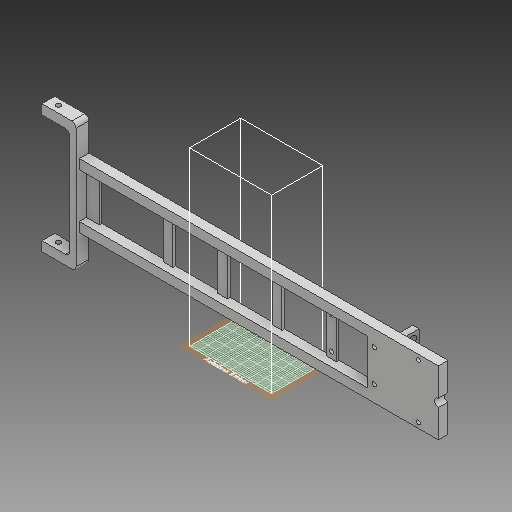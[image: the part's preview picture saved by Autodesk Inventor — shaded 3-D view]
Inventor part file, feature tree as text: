
AUTODESK INVENTOR PART (.ipt)
format: ipt  version: 2018 (Build 220112000, 112)  size: 669,184 bytes
history: native  units: mm
features: sketch x36, extrude x27, fillet x10, hole x6
ambient origin geometry x8: Origin, YZ Plane, XZ Plane, XY Plane, X Axis, Y Axis, Z Axis, Center Point
bodies: Solid1 (feature_tree)
feature tree (79):
  extrude  "Extrusion1"  Depth=50.0mm
  hole  "Hole1"  [1 undecoded]
  hole  "Hole2"  [1 undecoded]
  extrude  "Extrusion2"  Depth=25.0mm
  extrude  "Extrusion3"  Depth=25.0mm
  extrude  "Extrusion4"  Depth=5.0mm
  sketch  "Sketch7"  dims[d25=10.0mm d26=5.0mm]
  extrude  "Extrusion5"  Depth=5.0mm
  extrude  "Extrusion6"  Depth=35.0mm
  extrude  "Extrusion7"  Depth=35.0mm
  extrude  "Extrusion8"  Depth=35.0mm
  extrude  "Extrusion9"  Depth=2.0mm TaperAngle=0.0deg
  extrude  "Extrusion10"  Depth=7.5mm TaperAngle=0.0deg
  extrude  "Extrusion11"  Depth=10.0mm
  extrude  "Extrusion12"  Depth=7.5mm
  fillet  "Fillet1"  Radius=7.5mm
  fillet  "Fillet2"  Radius=25.0mm
  fillet  "Fillet3"  Radius=3.0mm
  fillet  "Fillet4"  Radius=3.2mm
  fillet  "Fillet5"  Radius=2.1mm
  fillet  "Fillet6"  Radius=5.5mm
  extrude  "Extrusion13"  Depth=92.5mm TaperAngle=0.0deg
  sketch  "Sketch17"  dims[d58=4.25mm d59=241.0mm d60=0.0mm]
  hole  "Hole3"  [1 undecoded]
  hole  "Hole4"  [1 undecoded]
  extrude  "Extrusion14"  Depth=5.0mm
  extrude  "Extrusion15"  Depth=91.25mm TaperAngle=0.0deg
  extrude  "Extrusion16"  Depth=30.0mm
  extrude  "Extrusion17"  Depth=2.5mm
  extrude  "Extrusion18"  Depth=14.55mm TaperAngle=0.0deg
  extrude  "Extrusion19"  Depth=0.1mm
  extrude  "Extrusion20"  Depth=3.25mm
  extrude  "Extrusion21"  Depth=3.25mm
  hole  "Hole5"  [1 undecoded]
  extrude  "Extrusion22"  Depth=2.0mm
  extrude  "Extrusion23"  Depth=15.0mm
  extrude  "Extrusion24"  Depth=10.0mm TaperAngle=0.0deg
  extrude  "Extrusion25"  Depth=2.0mm
  extrude  "Extrusion26"  Depth=100.0mm TaperAngle=0.0deg
  sketch  "Sketch34"  dims[d113=5.0mm d114=2.0mm d115=0.0mm]
  hole  "Hole6"  [1 undecoded]
  extrude  "Extrusion27"  Depth=5.5mm
  fillet  "Fillet7"  Radius=3.3mm
  fillet  "Fillet8"  Radius=3.3mm
  fillet  "Fillet9"  Radius=2.0mm
  fillet  "Fillet10"  Radius=5.5mm
  sketch  "Sketch1"  dims[d0=50.0mm d1=50.0mm]
  sketch  "Sketch2"  dims[d2=240.0mm d3=7.5mm]
  sketch  "Sketch3"  dims[d4=7.5mm d5=7.5mm d6=0.0mm]
  sketch  "Sketch4"  dims[d7=6.35mm d8=6.0mm d9=4.0mm d10=2.0mm d11=90.0deg d12=8.0mm d13=20.594885mm d14=25.0mm]
  sketch  "Sketch5"  dims[d15=3.3mm d16=6.0mm d17=4.0mm d18=2.0mm d19=90.0deg d20=8.0mm d21=20.594885mm d22=25.0mm]
  sketch  "Sketch6"  dims[d23=180.0deg d24=5.0mm]
  sketch  "Sketch8"  dims[d27=17.5mm d28=0.0mm d30=35.0mm]
  sketch  "Sketch9"  dims[d31=35.0mm d32=35.0mm]
  sketch  "Sketch10"  dims[d33=35.0mm d34=35.0mm]
  sketch  "Sketch11"  dims[d35=35.0mm d36=2.0mm d37=0.0mm]
  sketch  "Sketch12"  dims[d38=10.0mm d39=7.5mm d40=0.0mm]
  sketch  "Sketch13"  dims[d41=100.0mm d42=10.0mm]
  sketch  "Sketch14"  dims[d43=7.5mm d44=0.0mm d45=7.5mm d46=7.5mm d47=25.0mm d48=0.0mm d49=3.0mm d50=3.2mm d51=2.1mm d52=5.5mm]
  sketch  "Sketch15"  dims[d53=3.3mm d54=92.5mm d55=0.0mm]
  sketch  "Sketch16"  dims[d56=5.5mm d57=3.3mm]
  sketch  "Sketch18"  dims[d61=4.44mm d62=5.0mm]
  sketch  "Sketch19"  dims[d63=2.5mm d64=91.25mm d65=0.0mm]
  sketch  "Sketch20"  dims[d66=30.0mm d67=6.35mm]
  sketch  "Sketch21"  dims[d68=3.8mm d69=0.0mm d70=2.5mm]
  sketch  "Sketch22"  dims[d71=14.55mm d72=0.0mm d73=14.55mm d74=0.0mm]
  sketch  "Sketch23"  dims[d75=0.1mm d76=0.1mm]
  sketch  "Sketch24"  dims[d77=3.25mm d78=3.25mm]
  sketch  "Sketch25"  dims[d79=3.25mm d80=3.25mm]
  sketch  "Sketch26"  dims[d81=35.0mm d82=10.0mm]
  sketch  "Sketch27"  dims[d83=2.0mm d84=0.0mm d85=3.6mm]
  sketch  "Sketch28"  dims[d86=3.6mm]
  sketch  "Sketch29"  dims[d87=3.3mm d88=6.0mm d89=4.0mm d90=2.0mm d91=90.0deg d92=15.0mm d93=20.594885mm]
  sketch  "Sketch30"  dims[d94=3.3mm d95=6.0mm d96=4.0mm d97=2.0mm d98=90.0deg d99=15.0mm d100=20.594885mm d101=6.0mm]
  sketch  "Sketch31"  dims[d102=20.0mm d103=0.0mm d104=10.0mm d105=0.0mm]
  sketch  "Sketch32"  dims[d106=2.0mm d107=0.0mm d108=4.0mm]
  sketch  "Sketch33"  dims[d109=100.0mm d110=0.0mm d111=100.0mm d112=0.0mm]
  sketch  "Sketch35"  dims[d116=3.3mm d117=3.3mm d118=3.3mm d119=3.3mm d120=2.0mm d121=0.0mm d122=5.5mm d123=0.0mm]
  sketch  "Sketch36"  dims[d124=3.3mm d125=6.0mm d126=4.0mm d127=2.0mm d128=90.0deg d129=8.0mm d130=20.594885mm d131=42.0mm d132=17.0mm d133=21.0mm d135=8.5mm d136=15.825mm d137=3.5mm d138=21.0mm d139=3.3mm d140=3.3mm d141=3.3mm d142=10.0mm d143=0.0mm d144=7.5mm d145=0.0mm d146=100.0mm d147=0.0mm d148=42.0mm d149=7.5mm d150=7.5mm d151=0.0mm d152=34.0mm d153=7.5mm d154=75.0mm d155=25.0mm d156=5.0mm d157=5.0mm d158=7.5mm d159=0.0mm d160=4.0mm d161=2.0mm d162=4.0mm d163=4.0mm d164=6.0mm d165=4.0mm d166=2.0mm d167=90.0deg d168=800.0mm d169=20.594885mm d170=700.0mm d171=0.0mm d172=2.0mm d173=2.0mm d174=2.0mm d175=2.0mm]
note: 6 required parameter values undecoded (feature->parameter linkage not recoverable at this tier; creation-order binding heuristic only, values carry confidence <= 0.55)
